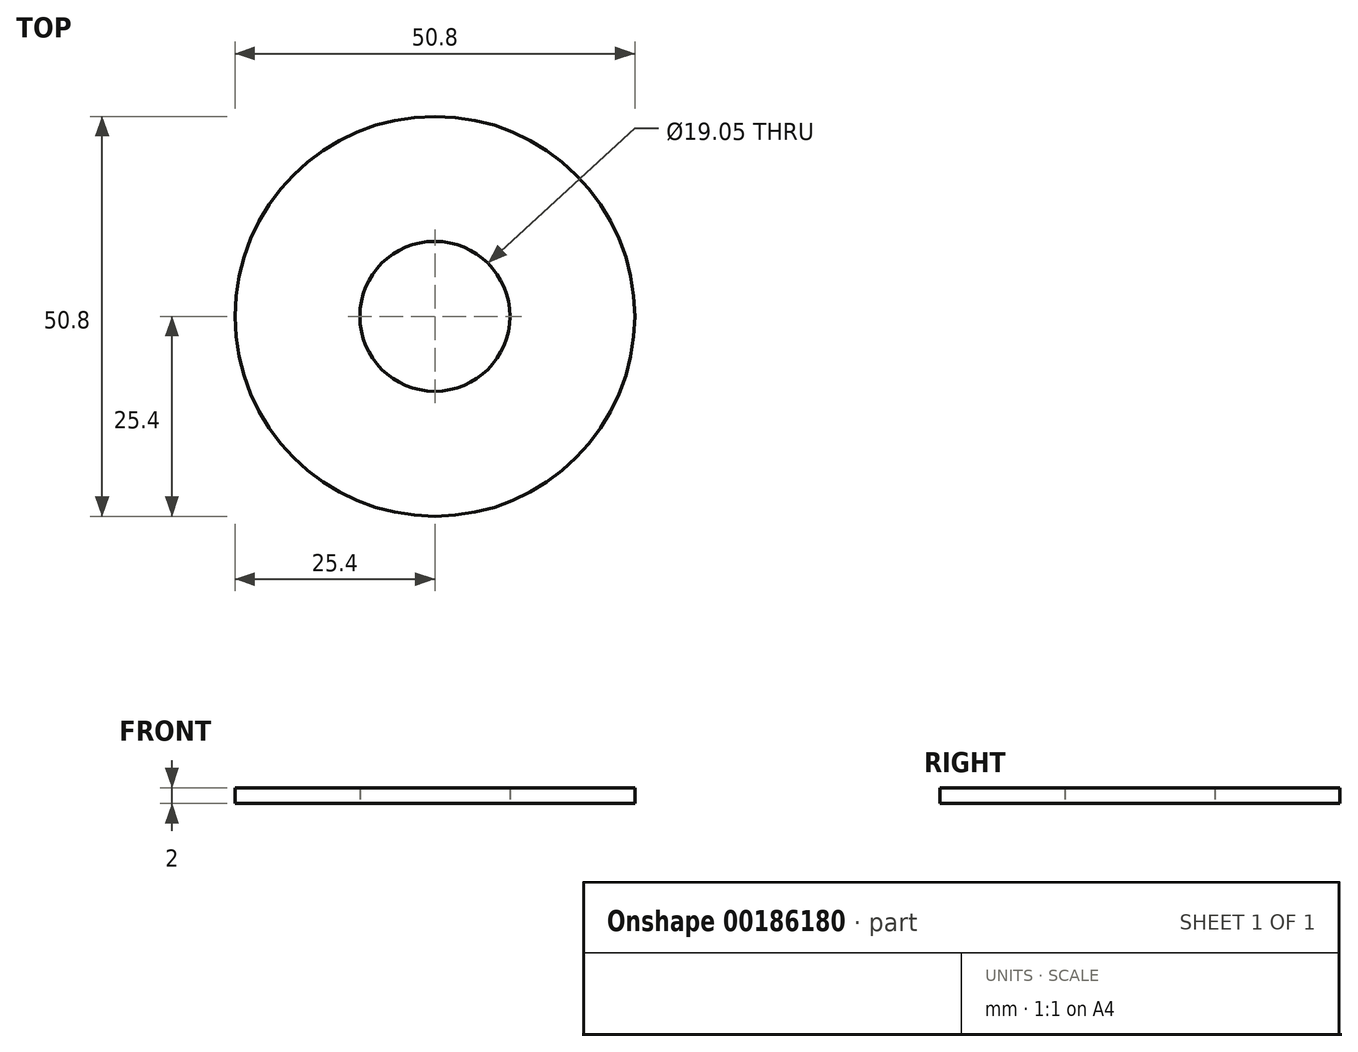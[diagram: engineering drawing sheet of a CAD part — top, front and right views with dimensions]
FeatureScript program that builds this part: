
annotation { "Feature Type Name" : "Feature", "Feature Type Description" : "" }
export const myFeature = defineFeature(function(context is Context, id is Id, definition is map)
    precondition{}
    {
        {
            var Q0;
            Q0=qCreatedBy(makeId("Top.planeOp"),FACE);
            var sketch = newSketch(context, id + "F0", { "sketchPlane" : qUnion([Q0])});
            skCircle(sketch, "E0", {"center": v(0, 0) * mm, "radius": 9.53 * mm});
            skCircle(sketch, "E1", {"center": v(0, 0) * mm, "radius": 25.4 * mm});
            skSolve(sketch);
        }
        {
            var Q0;
            Q0 = qSketchRegion(id + "F0", true);
            extrude(context, id + "F1", {"entities" : qUnion([Q0]), "depth" : 2 * mm});
        }
    });
